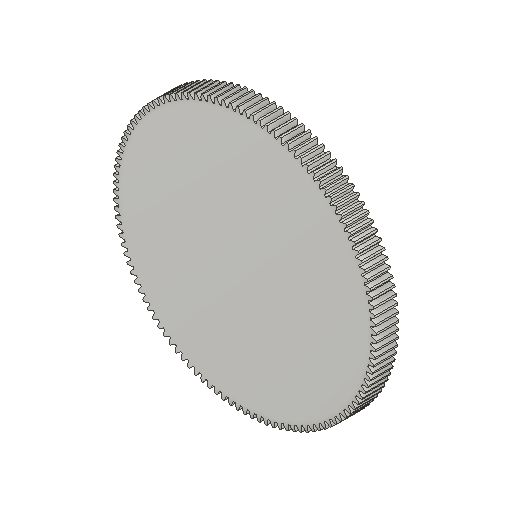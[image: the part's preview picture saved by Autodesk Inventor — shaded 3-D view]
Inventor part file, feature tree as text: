
AUTODESK INVENTOR PART (.ipt)
format: ipt  version: 2024 (Build 280153000, 153)  size: 564,736 bytes
history: native  units: mm (DEFAULTED — no unit token found)
features: plane x3, other x3, extrude x1, sketch x1
ambient origin geometry x8: Origin, YZ Plane, XZ Plane, XY Plane, X Axis, Y Axis, Z Axis, Center Point
bodies: Solid1 (feature_tree)
feature tree (8):
  extrude  "Extrusion1"  Depth=20.0mm TaperAngle=0.0deg
  plane  "Work Plane2"
  plane  "Work Plane8"
  plane  "Work Plane9"
  other  "Spur Gear"
  sketch  "Sketch1"  dims[d0=232.0mm d1=20.0mm d2=0.0mm d3=228.0mm d4=10.0mm d5=0.0mm d16=160.0mm d17=0.0mm d34=0.275578mm d39=0.0mm d41=0.0mm d43=160.0mm d46=160.0mm d47=0.0mm d48=0.0mm]
  other  "Srf1"
  other  "Pitch Diameter"
